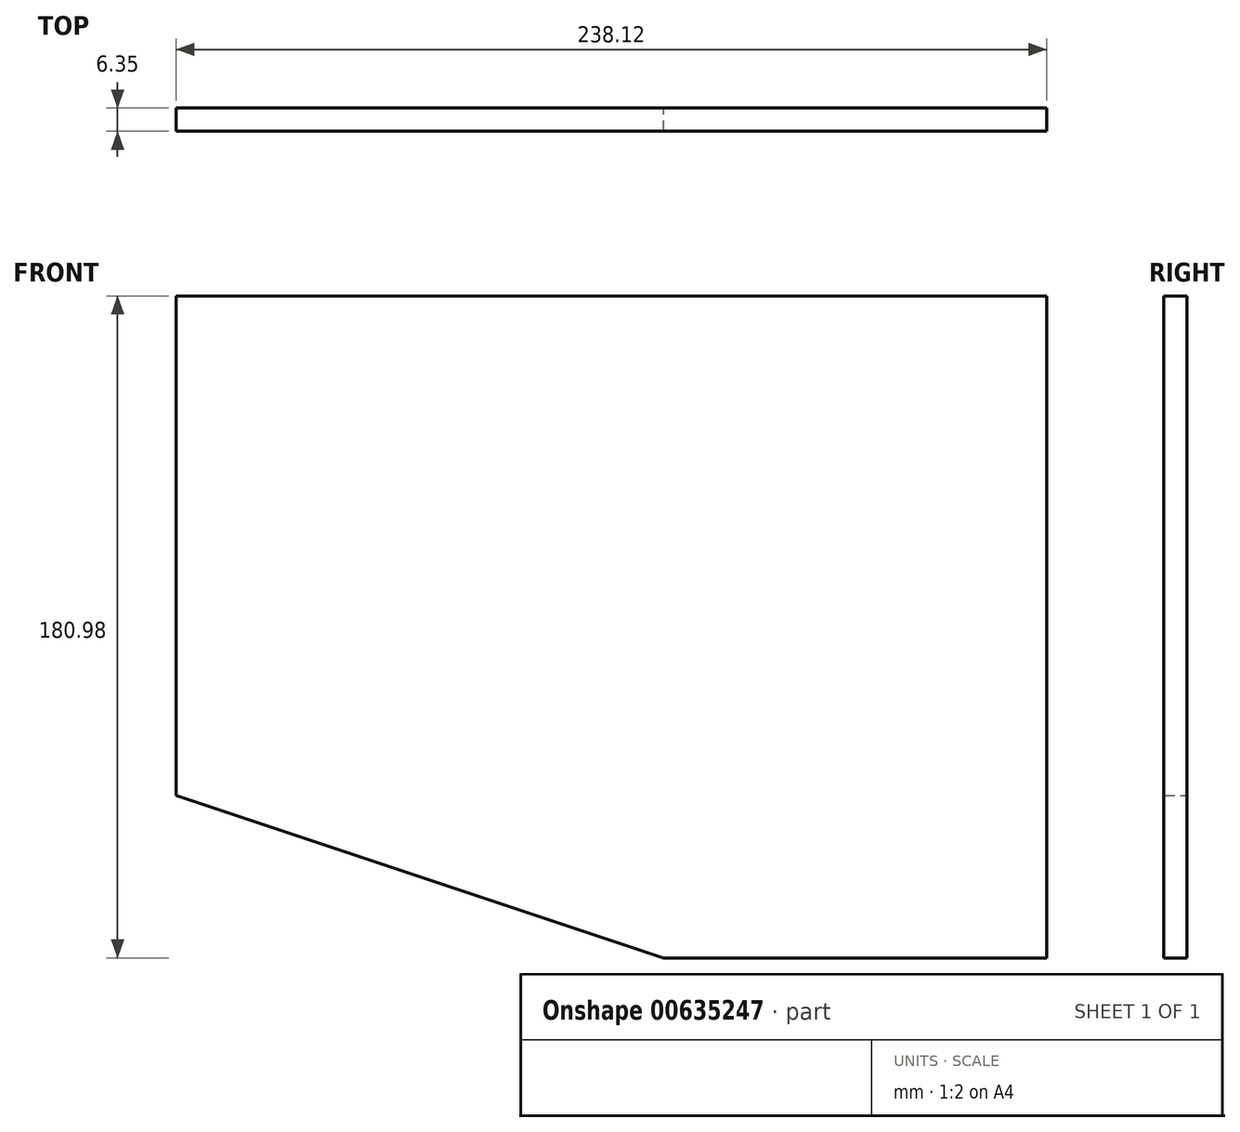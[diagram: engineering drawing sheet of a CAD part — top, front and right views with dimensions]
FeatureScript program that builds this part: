
annotation { "Feature Type Name" : "Feature", "Feature Type Description" : "" }
export const myFeature = defineFeature(function(context is Context, id is Id, definition is map)
    precondition{}
    {
        {
            var Q0;
            Q0=qCreatedBy(makeId("Front.planeOp"),FACE);
            var sketch = newSketch(context, id + "F0", { "sketchPlane" : qUnion([Q0])});
            skLineSegment(sketch, "E0.bottom", {"start": v(106.36, 90.49) * mm, "end": v(-106.36, 90.49) * mm});
            skLineSegment(sketch, "E0.top", {"start": v(106.36, -90.49) * mm, "end": v(-106.36, -90.49) * mm});
            skLineSegment(sketch, "E0.left", {"start": v(119.06, 77.79) * mm, "end": v(119.06, -77.79) * mm});
            skLineSegment(sketch, "E0.right", {"start": v(-119.06, 77.79) * mm, "end": v(-119.06, -77.79) * mm});
            skPoint(sketch, "E0.middle", {"position": v(0, 0) * mm});
            skPoint(sketch, "E1.visualSharp", {"position": v(-119.06, 90.49) * mm});
            skArc(sketch, "E1.filletArc", {"start": v(-106.36, 90.49) * mm, "mid": v(-115.34, 86.77) * mm, "end": v(-119.06, 77.79) * mm});
            skPoint(sketch, "E2.visualSharp", {"position": v(119.06, 90.49) * mm});
            skArc(sketch, "E2.filletArc", {"start": v(119.06, 77.79) * mm, "mid": v(115.34, 86.77) * mm, "end": v(106.36, 90.49) * mm});
            skPoint(sketch, "E3.visualSharp", {"position": v(-119.06, -90.49) * mm});
            skArc(sketch, "E3.filletArc", {"start": v(-119.06, -77.79) * mm, "mid": v(-115.34, -86.77) * mm, "end": v(-106.36, -90.49) * mm});
            skPoint(sketch, "E4.visualSharp", {"position": v(119.06, -90.49) * mm});
            skArc(sketch, "E4.filletArc", {"start": v(106.36, -90.49) * mm, "mid": v(115.34, -86.77) * mm, "end": v(119.06, -77.79) * mm});
            skLineSegment(sketch, "E5", {"start": v(-119.06, 77.79) * mm, "end": v(-119.06, 90.49) * mm});
            skLineSegment(sketch, "E6", {"start": v(-106.36, 90.49) * mm, "end": v(-119.06, 90.49) * mm});
            skLineSegment(sketch, "E7", {"start": v(106.36, 90.49) * mm, "end": v(119.06, 90.49) * mm});
            skLineSegment(sketch, "E8", {"start": v(119.06, 77.79) * mm, "end": v(119.06, 90.49) * mm});
            skLineSegment(sketch, "E9", {"start": v(119.06, -77.79) * mm, "end": v(119.06, -90.49) * mm});
            skLineSegment(sketch, "E10", {"start": v(106.36, -90.49) * mm, "end": v(119.06, -90.49) * mm});
            skLineSegment(sketch, "E11", {"start": v(-106.36, -90.49) * mm, "end": v(-119.06, -90.49) * mm});
            skLineSegment(sketch, "E12", {"start": v(-119.06, -77.79) * mm, "end": v(-119.06, -90.49) * mm});
            skSolve(sketch);
        }
        {
            var Q0;
            Q0 = qSketchRegion(id + "F0", true);
            extrude(context, id + "F1", {"entities" : qUnion([Q0]), "depth" : 6.35 * mm, "offsetDistance" : 25.4 * mm});
        }
        {
            var Q0;
            Q0=makeQuery(id+"F1.opExtrude","CAP_FACE",FACE,{"disambiguationData":[OSD([sQuery(id+"F0.wireOp",EDGE,"E0.bottom"),sQuery(id+"F0.wireOp",EDGE,"E0.top"),sQuery(id+"F0.wireOp",EDGE,"E0.left"),sQuery(id+"F0.wireOp",EDGE,"E0.right"),sQuery(id+"F0.wireOp",EDGE,"E5"),sQuery(id+"F0.wireOp",EDGE,"E6"),sQuery(id+"F0.wireOp",EDGE,"E7"),sQuery(id+"F0.wireOp",EDGE,"E8"),sQuery(id+"F0.wireOp",EDGE,"E9"),sQuery(id+"F0.wireOp",EDGE,"E10"),sQuery(id+"F0.wireOp",EDGE,"E11"),sQuery(id+"F0.wireOp",EDGE,"E12")])],"isStart":true});
            var sketch = newSketch(context, id + "F2", { "sketchPlane" : qUnion([Q0])});
            skLineSegment(sketch, "E13", {"start": v(119.06, -90.49) * mm, "end": v(119.06, -46.04) * mm});
            skLineSegment(sketch, "E14", {"start": v(119.06, -46.04) * mm, "end": v(-14.29, -90.49) * mm});
            skLineSegment(sketch, "E15", {"start": v(-14.29, -90.49) * mm, "end": v(119.06, -90.49) * mm});
            skSolve(sketch);
        }
        {
            var Q0;
            Q0 = qSketchRegion(id + "F2", true);
            extrude(context, id + "F3", {"entities" : qUnion([Q0]), "operationType" : NewBodyOperationType.REMOVE, "oppositeDirection" : true, "depth" : 25.4 * mm, "offsetDistance" : 25.4 * mm});
        }
    });
